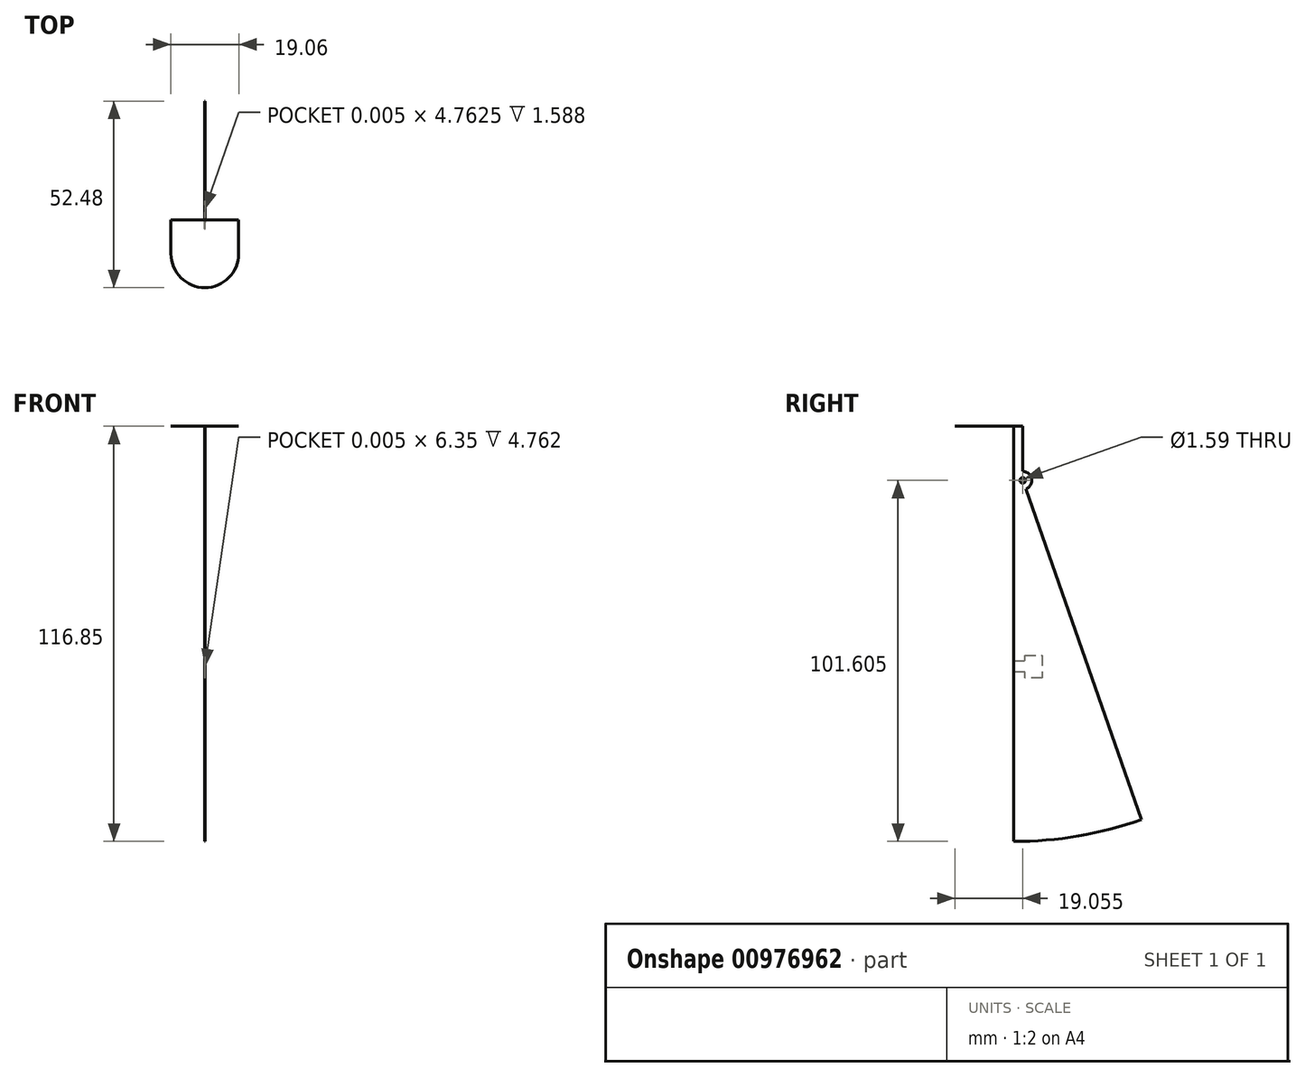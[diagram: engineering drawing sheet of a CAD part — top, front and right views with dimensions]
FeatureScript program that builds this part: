
annotation { "Feature Type Name" : "Feature", "Feature Type Description" : "" }
export const myFeature = defineFeature(function(context is Context, id is Id, definition is map)
    precondition{}
    {
        {
            var Q0;
            Q0=qCreatedBy(makeId("Front.planeOp"),FACE);
            var sketch = newSketch(context, id + "F0", { "sketchPlane" : qUnion([Q0])});
            skLineSegment(sketch, "E0", {"start": v(0, 55.3) * mm, "end": v(0, -71.7) * mm});
            skSolve(sketch);
        }
        {
            var Q0;
            Q0=sQuery(id+"F0.wireOp",VERTEX,"E0.start");
            var Q1;
            Q1=sQuery(id+"F0.wireOp",EDGE,"E0");
            cPlane(context, id + "F1", {"entities" : qUnion([Q0, Q1]), "cplaneType" : CPlaneType.LINE_POINT, "offset" : 25.4 * mm, "width" : 152.4 * mm, "height" : 152.4 * mm});
        }
        {
            var Q0;
            Q0=qCreatedBy(id+"F1.planeOp",FACE);
            var sketch = newSketch(context, id + "F2", { "sketchPlane" : qUnion([Q0])});
            skArc(sketch, "E1", {"start": v(-9.53, 0) * mm, "mid": v(0, 9.53) * mm, "end": v(9.53, 0) * mm});
            skLineSegment(sketch, "E2", {"start": v(-9.53, 0) * mm, "end": v(-9.53, -9.53) * mm});
            skLineSegment(sketch, "E3", {"start": v(-9.53, -9.53) * mm, "end": v(9.53, -9.53) * mm});
            skLineSegment(sketch, "E4", {"start": v(9.53, -9.53) * mm, "end": v(9.53, 0) * mm});
            skSolve(sketch);
        }
        {
            var Q0;
            Q0 = qSketchRegion(id + "F2", true);
            extrude(context, id + "F3", {"entities" : qUnion([Q0]), "oppositeDirection" : true, "depth" : 1 / 406.4 * mm, "offsetDistance" : 25.4 * mm});
        }
        {
            var Q0;
            Q0=qCreatedBy(makeId("Right.planeOp"),FACE);
            var sketch = newSketch(context, id + "F4", { "sketchPlane" : qUnion([Q0])});
            skLineSegment(sketch, "E5", {"start": v(9.53, 55.3) * mm, "end": v(9.53, 42.6) * mm});
            skLineSegment(sketch, "E6", {"start": v(42.95, -55.43) * mm, "end": v(10.36, 37.66) * mm});
            skLineSegment(sketch, "E7", {"start": v(6.99, 55.3) * mm, "end": v(9.53, 55.3) * mm});
            skCircle(sketch, "E8", {"center": v(9.53, 40.05) * mm, "radius": 2.54 * mm});
            skCircle(sketch, "E9", {"center": v(9.53, 40.05) * mm, "radius": 0.8 * mm});
            skLineSegment(sketch, "E10", {"start": v(6.99, 40.05) * mm, "end": v(6.99, -61.55) * mm});
            skLineSegment(sketch, "E11", {"start": v(6.99, -10.75) * mm, "end": v(10.16, -10.75) * mm});
            skLineSegment(sketch, "E12", {"start": v(10.16, -10.75) * mm, "end": v(10.16, -9.16) * mm});
            skLineSegment(sketch, "E13", {"start": v(10.16, -9.16) * mm, "end": v(14.92, -9.16) * mm});
            skLineSegment(sketch, "E14", {"start": v(14.92, -9.16) * mm, "end": v(14.92, -15.5) * mm});
            skLineSegment(sketch, "E15", {"start": v(14.92, -15.5) * mm, "end": v(10.16, -15.5) * mm});
            skLineSegment(sketch, "E16", {"start": v(10.16, -15.5) * mm, "end": v(10.16, -13.92) * mm});
            skLineSegment(sketch, "E17", {"start": v(10.16, -13.92) * mm, "end": v(6.99, -13.92) * mm});
            skLineSegment(sketch, "E18", {"start": v(6.99, -10.75) * mm, "end": v(6.99, -13.92) * mm});
            skLineSegment(sketch, "E19", {"start": v(6.99, 40.05) * mm, "end": v(6.99, 55.3) * mm});
            skArc(sketch, "E20", {"start": v(6.99, -61.55) * mm, "mid": v(25.22, -60) * mm, "end": v(42.95, -55.43) * mm});
            skSolve(sketch);
        }
        {
            var Q0;
            {var subQ1=sQuery(id+"F4.wireOp",EDGE,"E5");var subQ3=sQuery(id+"F4.wireOp",EDGE,"E6");var subQ14=sQuery(id+"F4.wireOp",EDGE,"E11");var subQ15=makeQuery(id+"F4.imprint","IMPRINT",EDGE,{"derivedFrom":subQ14});Q0=qUnion([makeQuery(id+"F4.imprint","IMPRINT",FACE,{"disambiguationData":[TD([[makeQuery(id+"F4.imprint","IMPRINT",EDGE,{"derivedFrom":subQ1}),-1.0]])]}),makeQuery(id+"F4.imprint","IMPRINT",FACE,{"disambiguationData":[TD([[subQ15,-1.0]])]}),makeQuery(id+"F4.imprint","IMPRINT",FACE,{"disambiguationData":[TD([[makeQuery(id+"F4.imprint","IMPRINT",EDGE,{"derivedFrom":subQ3}),1.0]])]}),makeQuery(id+"F4.imprint","IMPRINT",FACE,{"disambiguationData":[TD([[makeQuery(id+"F4.imprint","IMPRINT",EDGE,{"derivedFrom":sQuery(id+"F4.wireOp",EDGE,"E9")}),-1.0]])]})]);}
            extrude(context, id + "F5", {"entities" : qUnion([Q0]), "operationType" : NewBodyOperationType.ADD, "endBound" : BoundingType.SYMMETRIC, "oppositeDirection" : true, "depth" : 1 / 101.6 * mm, "offsetDistance" : 25.4 * mm});
        }
        {
            var Q0;
            {var subQ0=sQuery(id+"F4.wireOp",EDGE,"E11");Q0=makeQuery(id+"F4.imprint","IMPRINT",FACE,{"disambiguationData":[TD([[makeQuery(id+"F4.imprint","IMPRINT",EDGE,{"derivedFrom":subQ0}),-1.0]])]});}
            extrude(context, id + "F6", {"entities" : qUnion([Q0]), "operationType" : NewBodyOperationType.REMOVE, "endBound" : BoundingType.SYMMETRIC, "depth" : 1 / 203.2 * mm, "offsetDistance" : 25.4 * mm});
        }
    });
